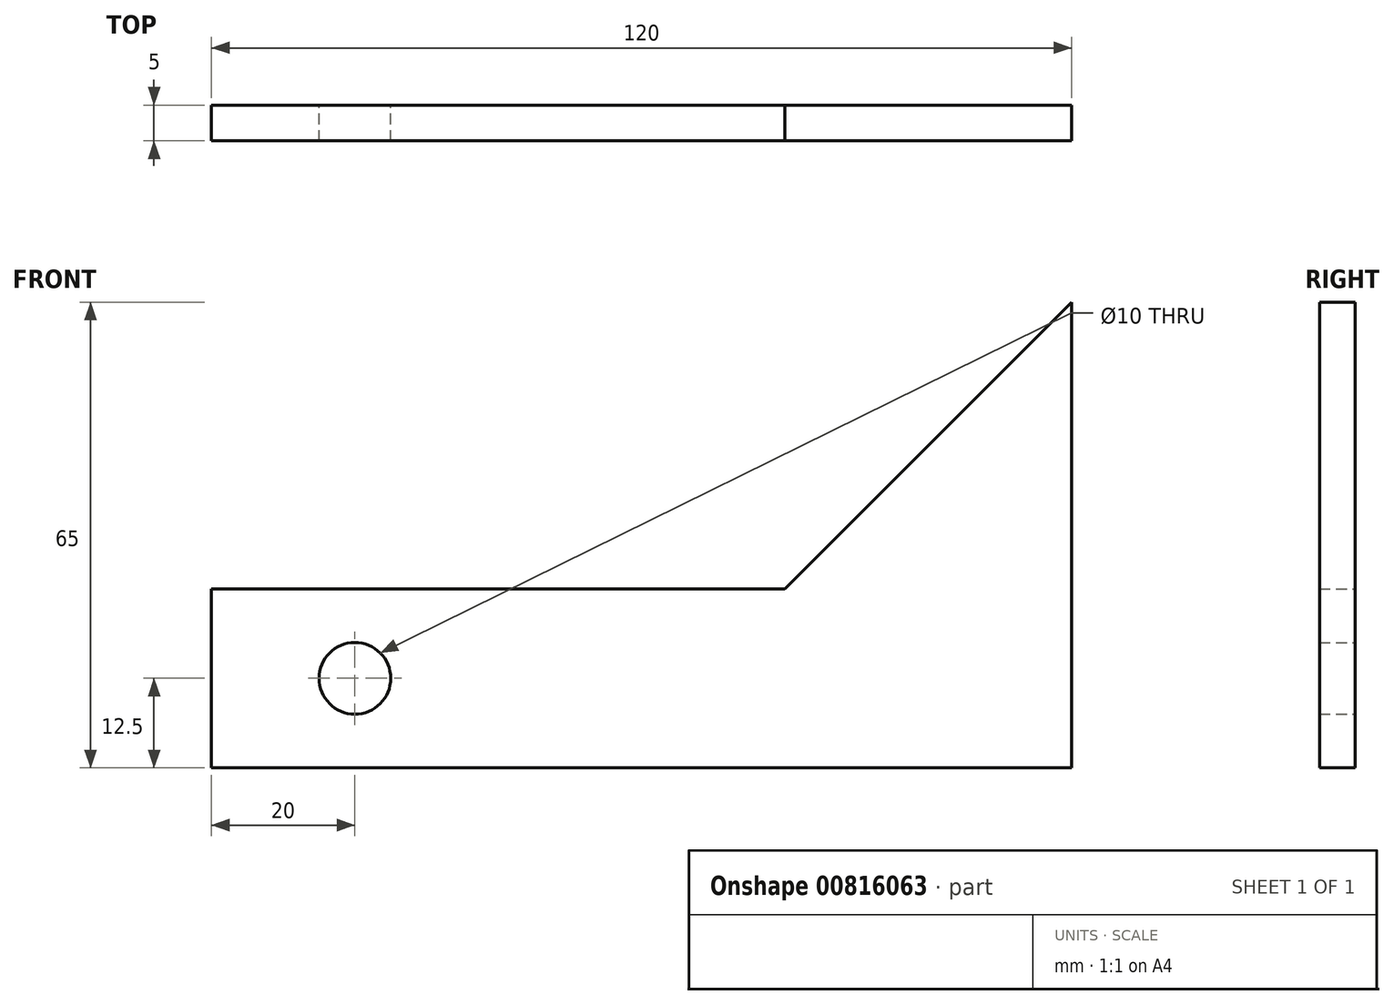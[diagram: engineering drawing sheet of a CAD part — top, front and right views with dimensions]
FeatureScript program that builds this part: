
annotation { "Feature Type Name" : "Feature", "Feature Type Description" : "" }
export const myFeature = defineFeature(function(context is Context, id is Id, definition is map)
    precondition{}
    {
        {
            var Q0;
            Q0=qCreatedBy(makeId("Front.planeOp"),FACE);
            var sketch = newSketch(context, id + "F0", { "sketchPlane" : qUnion([Q0])});
            skCircle(sketch, "E0", {"center": v(0, 0) * mm, "radius": 5 * mm});
            skLineSegment(sketch, "E1.bottom", {"start": v(-20, 12.5) * mm, "end": v(100, 12.5) * mm});
            skLineSegment(sketch, "E1.top", {"start": v(-20, -12.5) * mm, "end": v(100, -12.5) * mm});
            skLineSegment(sketch, "E1.left", {"start": v(-20, 12.5) * mm, "end": v(-20, -12.5) * mm});
            skLineSegment(sketch, "E1.right", {"start": v(100, 12.5) * mm, "end": v(100, -12.5) * mm});
            skPoint(sketch, "E2", {"position": v(-20, 0) * mm});
            skLineSegment(sketch, "E3", {"start": v(100, 12.5) * mm, "end": v(100, 52.5) * mm});
            skLineSegment(sketch, "E4", {"start": v(100, 52.5) * mm, "end": v(60, 12.5) * mm});
            skSolve(sketch);
        }
        {
            var Q0;
            Q0=makeQuery(id+"F0.imprint","IMPRINT",FACE,{"disambiguationData":[TD([[makeQuery(id+"F0.imprint","IMPRINT",EDGE,{"derivedFrom":sQuery(id+"F0.wireOp",EDGE,"E0")}),-1.0]])]});
            var Q1;
            {var subQ0=sQuery(id+"F0.wireOp",EDGE,"E3");Q1=makeQuery(id+"F0.imprint","IMPRINT",FACE,{"disambiguationData":[TD([[makeQuery(id+"F0.imprint","IMPRINT",EDGE,{"derivedFrom":subQ0}),1.0]])]});}
            extrude(context, id + "F1", {"entities" : qUnion([Q0, Q1]), "depth" : 5 * mm, "offsetDistance" : 25 * mm});
        }
    });
